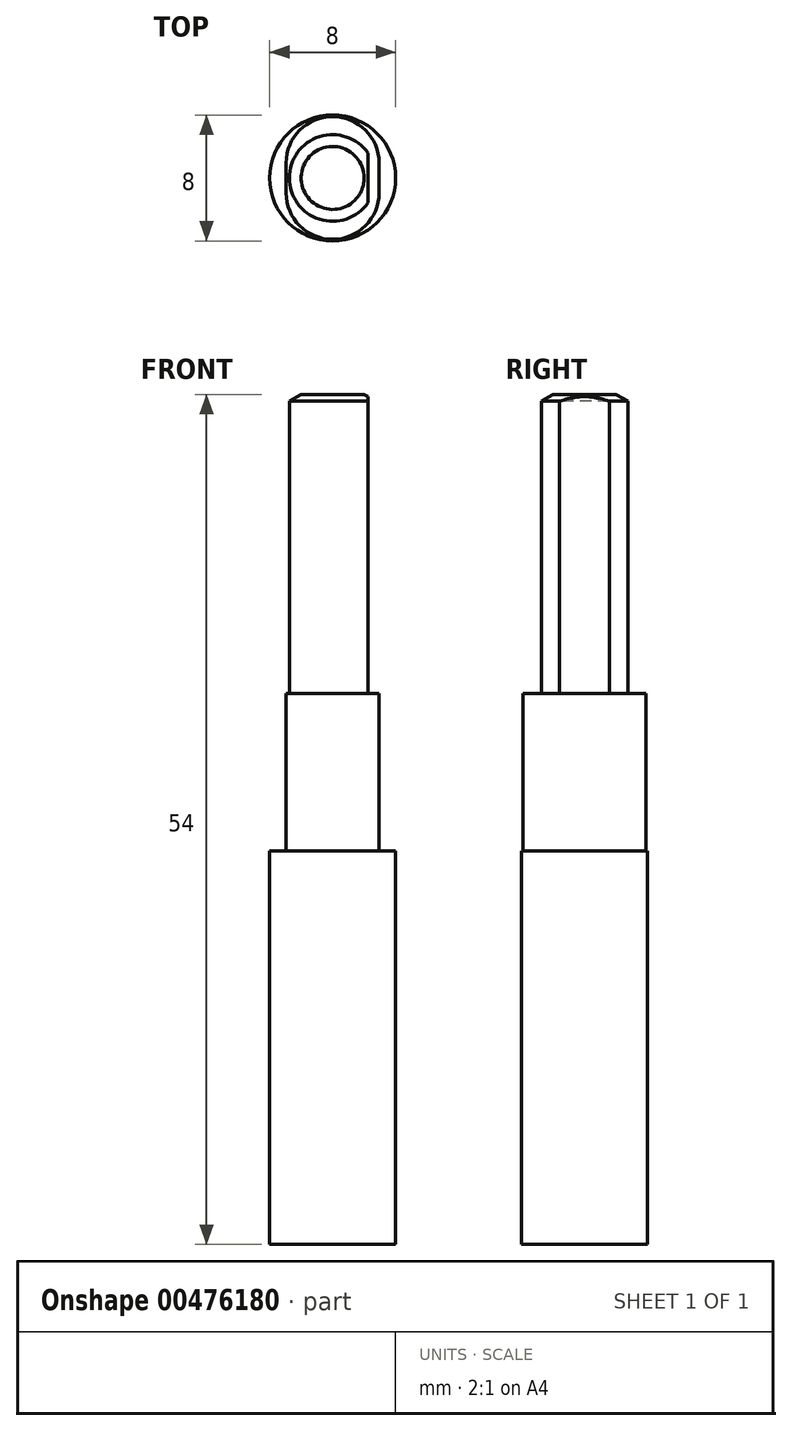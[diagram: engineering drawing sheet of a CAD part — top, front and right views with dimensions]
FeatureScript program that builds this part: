
annotation { "Feature Type Name" : "Feature", "Feature Type Description" : "" }
export const myFeature = defineFeature(function(context is Context, id is Id, definition is map)
    precondition{}
    {
        {
            var Q0;
            Q0=qCreatedBy(makeId("Top.planeOp"),FACE);
            var sketch = newSketch(context, id + "F0", { "sketchPlane" : qUnion([Q0])});
            skCircle(sketch, "E0", {"center": v(0, 0) * mm, "radius": 4 * mm});
            skSolve(sketch);
        }
        {
            var Q0;
            Q0 = qSketchRegion(id + "F0", true);
            extrude(context, id + "F1", {"entities" : qUnion([Q0]), "depth" : 25 * mm});
        }
        {
            var Q0;
            Q0=makeQuery(id+"F1.opExtrude","CAP_FACE",FACE,{"disambiguationData":[OSD([sQuery(id+"F0.wireOp",EDGE,"E0")])],"isStart":false});
            var sketch = newSketch(context, id + "F2", { "sketchPlane" : qUnion([Q0])});
            skLineSegment(sketch, "E1.bottom", {"start": v(0, -3.9) * mm, "end": v(0, -3.9) * mm});
            skLineSegment(sketch, "E1.top", {"start": v(0, 3.9) * mm, "end": v(0, 3.9) * mm});
            skLineSegment(sketch, "E1.left", {"start": v(2.95, -0.95) * mm, "end": v(2.95, 0.95) * mm});
            skLineSegment(sketch, "E1.right", {"start": v(-2.95, -0.95) * mm, "end": v(-2.95, 0.95) * mm});
            skPoint(sketch, "E1.middle", {"position": v(0, 0) * mm});
            skPoint(sketch, "E2.visualSharp", {"position": v(2.95, 3.9) * mm});
            skArc(sketch, "E2.filletArc", {"start": v(2.95, 0.95) * mm, "mid": v(2.09, 3.04) * mm, "end": v(0, 3.9) * mm});
            skPoint(sketch, "E3.visualSharp", {"position": v(-2.95, 3.9) * mm});
            skArc(sketch, "E3.filletArc", {"start": v(0, 3.9) * mm, "mid": v(-2.09, 3.04) * mm, "end": v(-2.95, 0.95) * mm});
            skPoint(sketch, "E4.visualSharp", {"position": v(-2.95, -3.9) * mm});
            skArc(sketch, "E4.filletArc", {"start": v(-2.95, -0.95) * mm, "mid": v(-2.09, -3.04) * mm, "end": v(0, -3.9) * mm});
            skPoint(sketch, "E5.visualSharp", {"position": v(2.95, -3.9) * mm});
            skArc(sketch, "E5.filletArc", {"start": v(0, -3.9) * mm, "mid": v(2.09, -3.04) * mm, "end": v(2.95, -0.95) * mm});
            skSolve(sketch);
        }
        {
            var Q0;
            Q0=makeQuery(id+"F2.imprint","IMPRINT",FACE,{"disambiguationData":[TD([[makeQuery(id+"F2.imprint","IMPRINT",EDGE,{"derivedFrom":sQuery(id+"F2.wireOp",EDGE,"E1.left")}),1.0]])]});
            extrude(context, id + "F3", {"entities" : qUnion([Q0]), "operationType" : NewBodyOperationType.ADD, "depth" : 10 * mm});
        }
        {
            var Q0;
            Q0=makeQuery(id+"F3.opExtrude","CAP_FACE",FACE,{"disambiguationData":[OSD([sQuery(id+"F2.wireOp",EDGE,"E1.left"),sQuery(id+"F2.wireOp",EDGE,"E1.right"),sQuery(id+"F2.wireOp",EDGE,"E2.filletArc"),sQuery(id+"F2.wireOp",EDGE,"E3.filletArc"),sQuery(id+"F2.wireOp",EDGE,"E4.filletArc"),sQuery(id+"F2.wireOp",EDGE,"E5.filletArc")])],"isStart":false});
            var sketch = newSketch(context, id + "F4", { "sketchPlane" : qUnion([Q0])});
            skCircle(sketch, "E6", {"center": v(0, 0) * mm, "radius": 2.75 * mm});
            skSolve(sketch);
        }
        {
            var Q0;
            Q0 = qSketchRegion(id + "F4", true);
            extrude(context, id + "F5", {"entities" : qUnion([Q0]), "operationType" : NewBodyOperationType.ADD, "depth" : 19 * mm});
        }
        {
            var Q0;
            Q0=makeQuery(id+"F5.opExtrude","CAP_EDGE",EDGE,{"disambiguationData":[OSD([sQuery(id+"F4.wireOp",EDGE,"E6")])],"isStart":false});
            chamfer(context, id + "F6", {"entities" : qUnion([Q0]), "chamferType" : ChamferType.OFFSET_ANGLE, "width" : .75 * mm, "oppositeDirection" : false, "angle" : 30 * degree, "tangentPropagation" : true});
        }
        {
            var Q0;
            Q0=makeQuery(id+"F5.opExtrude","CAP_FACE",FACE,{"disambiguationData":[OSD([sQuery(id+"F4.wireOp",EDGE,"E6")])],"isStart":false});
            var sketch = newSketch(context, id + "F7", { "sketchPlane" : qUnion([Q0])});
            skLineSegment(sketch, "E7", {"start": v(0, 0) * mm, "end": v(2.25, 0) * mm, "construction": true});
            skLineSegment(sketch, "E8", {"start": v(2.25, 0) * mm, "end": v(2.25, 2.96) * mm});
            skLineSegment(sketch, "E9", {"start": v(2.25, 2.96) * mm, "end": v(3.5, 2.96) * mm});
            skLineSegment(sketch, "E10", {"start": v(3.5, 2.96) * mm, "end": v(3.5, -3.4) * mm});
            skLineSegment(sketch, "E11", {"start": v(3.5, -3.4) * mm, "end": v(2.25, -3.4) * mm});
            skLineSegment(sketch, "E12", {"start": v(2.25, -3.4) * mm, "end": v(2.25, 0) * mm});
            skSolve(sketch);
        }
        {
            var Q0;
            {var subQ1=sQuery(id+"F7.wireOp",EDGE,"E9");Q0=makeQuery(id+"F7.imprint","IMPRINT",FACE,{"disambiguationData":[TD([[makeQuery(id+"F7.imprint","IMPRINT",EDGE,{"derivedFrom":subQ1}),-1.0]])]});}
            var Q1;
            {var subQ0=sQuery(id+"F7.wireOp",EDGE,"E12");var subQ1=sQuery(id+"F7.wireOp",EDGE,"E8");var subQ2=makeQuery(id+"F7.imprint","INTERSECT",VERTEX,{"derivedFrom":[subQ1,subQ0]});Q1=makeQuery(id+"F7.imprint","IMPRINT",FACE,{"disambiguationData":[TD([[makeQuery(id+"F7.imprint","IMPRINT",EDGE,{"disambiguationData":[TD([[subQ2,-1.0]])],"derivedFrom":subQ1}),-1.0]])]});}
            extrude(context, id + "F8", {"entities" : qUnion([Q0, Q1]), "operationType" : NewBodyOperationType.REMOVE, "oppositeDirection" : true, "depth" : 19 * mm});
        }
    });
